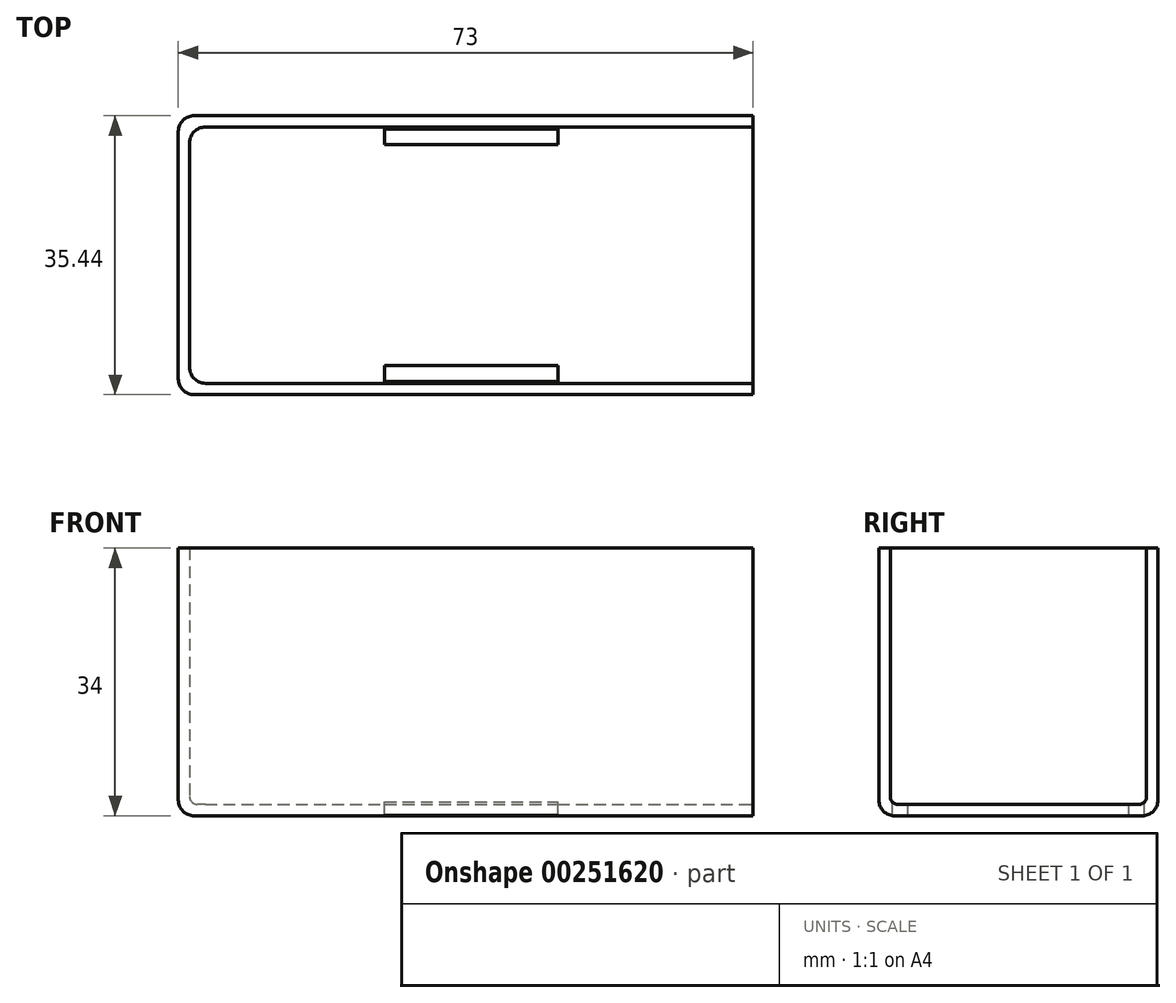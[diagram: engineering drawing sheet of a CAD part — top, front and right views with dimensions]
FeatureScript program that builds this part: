
annotation { "Feature Type Name" : "Feature", "Feature Type Description" : "" }
export const myFeature = defineFeature(function(context is Context, id is Id, definition is map)
    precondition{}
    {
        {
            var Q0;
            Q0=qCreatedBy(makeId("Top.planeOp"),FACE);
            var sketch = newSketch(context, id + "F0", { "sketchPlane" : qUnion([Q0])});
            skLineSegment(sketch, "E0.bottom", {"start": v(-37.22, 17.72) * mm, "end": v(37.22, 17.72) * mm});
            skLineSegment(sketch, "E0.top", {"start": v(-37.22, -17.72) * mm, "end": v(37.22, -17.72) * mm});
            skLineSegment(sketch, "E0.left", {"start": v(-37.22, 17.72) * mm, "end": v(-37.22, -17.72) * mm});
            skLineSegment(sketch, "E0.right", {"start": v(37.22, 17.72) * mm, "end": v(37.22, -17.72) * mm});
            skPoint(sketch, "E0.middle", {"position": v(0, 0) * mm});
            skSolve(sketch);
        }
        {
            var Q0;
            Q0=qSketchRegion(id+"F0",true);
            extrude(context, id + "F1", {"entities" : qUnion([Q0]), "depth" : 34 * mm});
        }
        {
            var Q0;
            Q0=makeQuery(id+"F1.opExtrude","CAP_FACE",FACE,{"disambiguationData":[OSD([sQuery(id+"F0.wireOp",EDGE,"E0.bottom"),sQuery(id+"F0.wireOp",EDGE,"E0.top"),sQuery(id+"F0.wireOp",EDGE,"E0.left"),sQuery(id+"F0.wireOp",EDGE,"E0.right")])],"isStart":false});
            shell(context, id + "F2", {"entities" : qUnion([Q0]), "thickness" : 1.44 * mm});
        }
        {
            var Q0;
            Q0=makeQuery(id+"F1.opExtrude","SWEPT_FACE",FACE,{"disambiguationData":[OSD([sQuery(id+"F0.wireOp",EDGE,"E0.right")])]});
            extrude(context, id + "F3", {"entities" : qUnion([Q0]), "operationType" : NewBodyOperationType.REMOVE, "oppositeDirection" : true, "depth" : 1.44 * mm});
        }
        {
            var Q0;
            Q0=makeQuery(id+"F2.opShell","OFFSET_EDGE",EDGE,{"disambiguationData":[OSD([sQuery(id+"F0.wireOp",EDGE,"E0.top"),sQuery(id+"F0.wireOp",EDGE,"E0.left")])]});
            var Q1;
            Q1=makeQuery(id+"F2.opShell","OFFSET_EDGE",EDGE,{"disambiguationData":[OSD([sQuery(id+"F0.wireOp",EDGE,"E0.bottom"),sQuery(id+"F0.wireOp",EDGE,"E0.left")])]});
            var Q2;
            Q2=makeQuery(id+"F1.opExtrude","SWEPT_EDGE",EDGE,{"disambiguationData":[OSD([sQuery(id+"F0.wireOp",EDGE,"E0.bottom"),sQuery(id+"F0.wireOp",EDGE,"E0.left")])]});
            var Q3;
            Q3=makeQuery(id+"F1.opExtrude","SWEPT_EDGE",EDGE,{"disambiguationData":[OSD([sQuery(id+"F0.wireOp",EDGE,"E0.top"),sQuery(id+"F0.wireOp",EDGE,"E0.left")])]});
            fillet(context, id + "F4", {"entities" : qUnion([Q0, Q1, Q2, Q3]), "radius" : 2 * mm, "tangentPropagation" : true, "allowEdgeOverflow" : false});
        }
        {
            var Q0;
            Q0=makeQuery(id+"F1.opExtrude","CAP_EDGE",EDGE,{"disambiguationData":[OSD([sQuery(id+"F0.wireOp",EDGE,"E0.left")])],"isStart":true});
            var Q1;
            Q1=makeQuery(id+"F1.opExtrude","CAP_EDGE",EDGE,{"disambiguationData":[OSD([sQuery(id+"F0.wireOp",EDGE,"E0.top")])],"isStart":true});
            var Q2;
            Q2=makeQuery(id+"F1.opExtrude","CAP_EDGE",EDGE,{"disambiguationData":[OSD([sQuery(id+"F0.wireOp",EDGE,"E0.bottom")])],"isStart":true});
            fillet(context, id + "F5", {"entities" : qUnion([Q0, Q1, Q2]), "radius" : 2 * mm, "allowEdgeOverflow" : false});
        }
        {
            var Q0;
            Q0=makeQuery(id+"F2.opShell","OFFSET_FACE",FACE,{"disambiguationData":[OSD([sQuery(id+"F0.wireOp",EDGE,"E0.bottom"),sQuery(id+"F0.wireOp",EDGE,"E0.top"),sQuery(id+"F0.wireOp",EDGE,"E0.left"),sQuery(id+"F0.wireOp",EDGE,"E0.right")])]});
            var sketch = newSketch(context, id + "F6", { "sketchPlane" : qUnion([Q0])});
            skLineSegment(sketch, "E1.bottom", {"start": v(-11, 14.03) * mm, "end": v(11, 14.03) * mm});
            skLineSegment(sketch, "E1.top", {"start": v(-11, 16.03) * mm, "end": v(11, 16.03) * mm});
            skLineSegment(sketch, "E1.left", {"start": v(-11, 14.03) * mm, "end": v(-11, 16.03) * mm});
            skLineSegment(sketch, "E1.right", {"start": v(11, 14.03) * mm, "end": v(11, 16.03) * mm});
            skPoint(sketch, "E1.middle", {"position": v(0, 15.03) * mm});
            skLineSegment(sketch, "E2.MirrorCS", {"start": v(-11, -14.03) * mm, "end": v(11, -14.03) * mm});
            skLineSegment(sketch, "E3.MirrorCS", {"start": v(-11, -14.03) * mm, "end": v(-11, -16.03) * mm});
            skLineSegment(sketch, "E4.MirrorCS", {"start": v(-11, -16.03) * mm, "end": v(11, -16.03) * mm});
            skLineSegment(sketch, "E5.MirrorCS", {"start": v(11, -14.03) * mm, "end": v(11, -16.03) * mm});
            skSolve(sketch);
        }
        {
            var Q0;
            Q0=qSketchRegion(id+"F6",true);
            extrude(context, id + "F7", {"entities" : qUnion([Q0]), "operationType" : NewBodyOperationType.REMOVE, "endBound" : BoundingType.THROUGH_ALL, "oppositeDirection" : true, "depth" : 25 * mm});
        }
        {
            var Q0;
            {var subQ0=sQuery(id+"F0.wireOp",EDGE,"E0.top");Q0=makeQuery(id+"F2.opShell","OFFSET_EDGE",EDGE,{"disambiguationData":[OSD([subQ0]),TDD([makeQuery(id+"F1.opExtrude","CAP_EDGE",EDGE,{"disambiguationData":[OSD([subQ0])],"isStart":true})])]});}
            fillet(context, id + "F8", {"entities" : qUnion([Q0]), "radius" : 1 * mm, "tangentPropagation" : true, "allowEdgeOverflow" : false});
        }
    });
